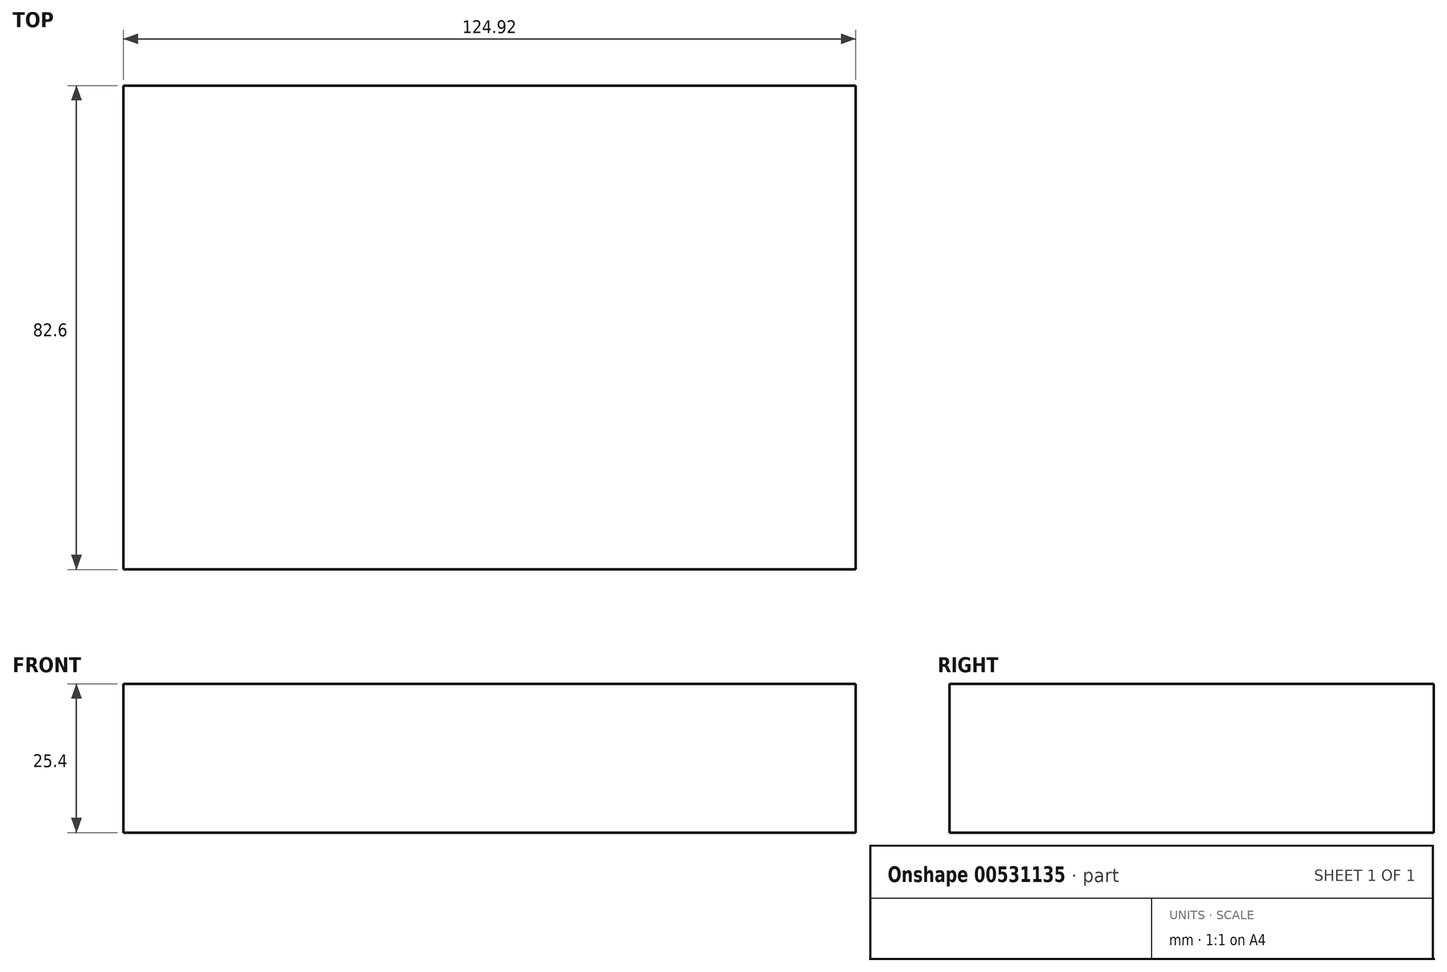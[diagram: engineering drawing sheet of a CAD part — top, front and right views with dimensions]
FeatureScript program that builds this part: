
annotation { "Feature Type Name" : "Feature", "Feature Type Description" : "" }
export const myFeature = defineFeature(function(context is Context, id is Id, definition is map)
    precondition{}
    {
        {
            var Q0;
            Q0=qCreatedBy(makeId("Top.planeOp"),FACE);
            var sketch = newSketch(context, id + "F0", { "sketchPlane" : qUnion([Q0])});
            skLineSegment(sketch, "E0.bottom", {"start": v(62.46, 41.3) * mm, "end": v(-62.46, 41.3) * mm});
            skLineSegment(sketch, "E0.top", {"start": v(62.46, -41.3) * mm, "end": v(-62.46, -41.3) * mm});
            skLineSegment(sketch, "E0.left", {"start": v(62.46, 41.3) * mm, "end": v(62.46, -41.3) * mm});
            skLineSegment(sketch, "E0.right", {"start": v(-62.46, 41.3) * mm, "end": v(-62.46, -41.3) * mm});
            skPoint(sketch, "E0.middle", {"position": v(0, 0) * mm});
            skSolve(sketch);
        }
        {
            var Q0;
            Q0=makeQuery(id+"F0.imprint","IMPRINT",FACE,{"disambiguationData":[TD([[makeQuery(id+"F0.imprint","IMPRINT",EDGE,{"derivedFrom":sQuery(id+"F0.wireOp",EDGE,"E0.bottom")}),1.0]])]});
            extrude(context, id + "F1", {"entities" : qUnion([Q0]), "depth" : 25.4 * mm, "offsetDistance" : 25.4 * mm});
        }
    });
